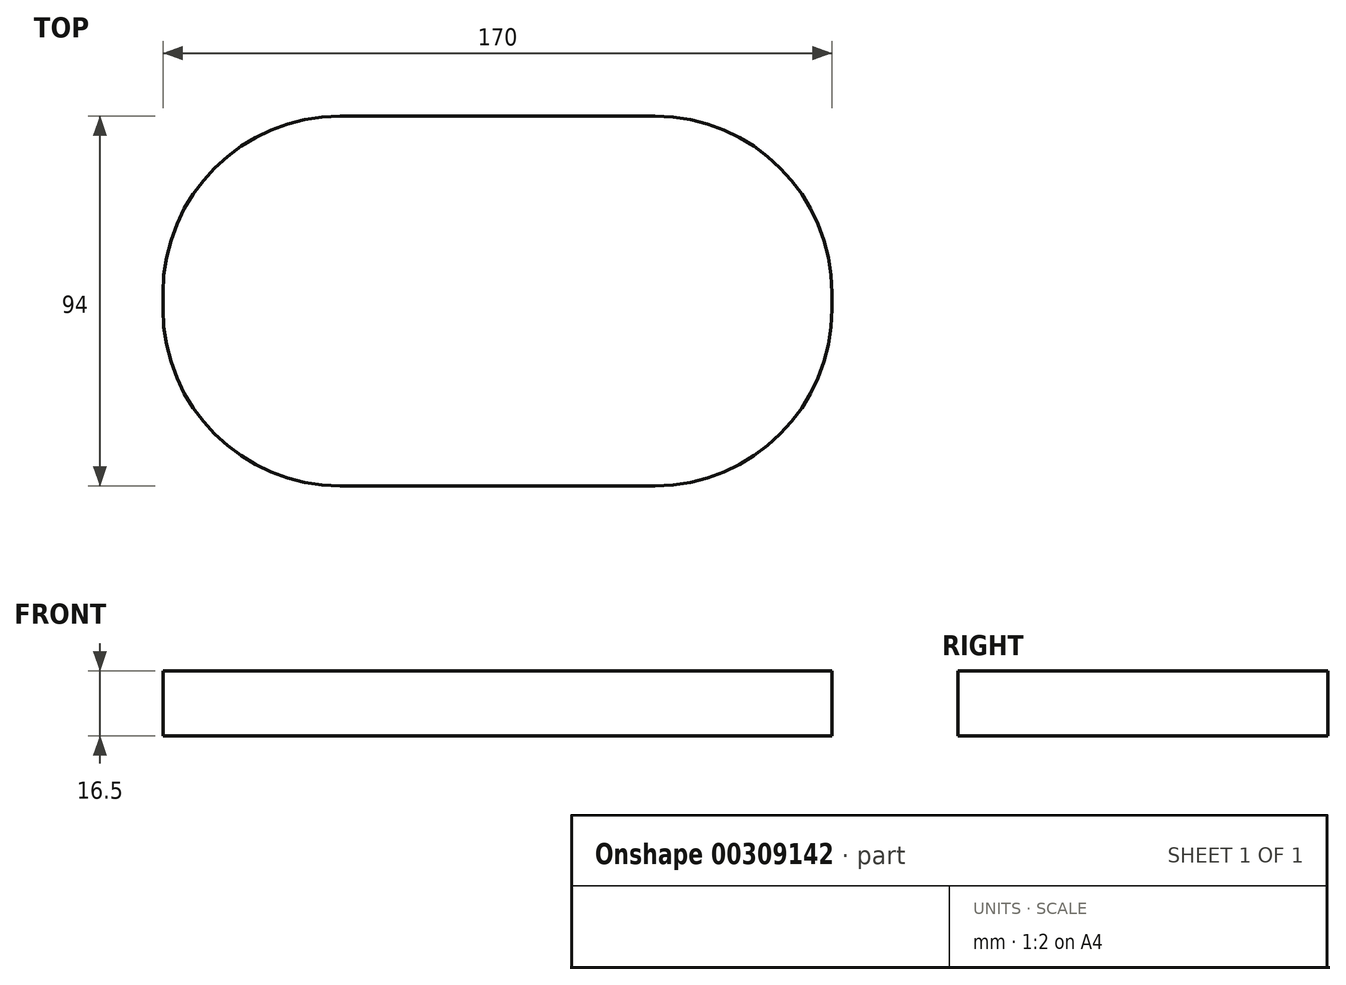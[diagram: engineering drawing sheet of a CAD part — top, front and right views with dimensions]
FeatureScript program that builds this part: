
annotation { "Feature Type Name" : "Feature", "Feature Type Description" : "" }
export const myFeature = defineFeature(function(context is Context, id is Id, definition is map)
    precondition{}
    {
        {
            var Q0;
            Q0=qCreatedBy(makeId("Top.planeOp"),FACE);
            var sketch = newSketch(context, id + "F0", { "sketchPlane" : qUnion([Q0])});
            skLineSegment(sketch, "E0.bottom", {"start": v(44.5, -51.5) * mm, "end": v(-44.5, -51.5) * mm});
            skLineSegment(sketch, "E0.top", {"start": v(44.5, 51.5) * mm, "end": v(-44.5, 51.5) * mm});
            skLineSegment(sketch, "E0.left", {"start": v(89.5, -6.5) * mm, "end": v(89.5, 6.5) * mm});
            skLineSegment(sketch, "E0.right", {"start": v(-89.5, -6.5) * mm, "end": v(-89.5, 6.5) * mm});
            skPoint(sketch, "E0.middle", {"position": v(0, 0) * mm});
            skPoint(sketch, "E1.visualSharp", {"position": v(89.5, 51.5) * mm});
            skArc(sketch, "E1.filletArc", {"start": v(89.5, 6.5) * mm, "mid": v(76.32, 38.32) * mm, "end": v(44.5, 51.5) * mm});
            skPoint(sketch, "E2.visualSharp", {"position": v(89.5, -51.5) * mm});
            skArc(sketch, "E2.filletArc", {"start": v(44.5, -51.5) * mm, "mid": v(76.32, -38.32) * mm, "end": v(89.5, -6.5) * mm});
            skPoint(sketch, "E3.visualSharp", {"position": v(-89.5, -51.5) * mm});
            skArc(sketch, "E3.filletArc", {"start": v(-89.5, -6.5) * mm, "mid": v(-76.32, -38.32) * mm, "end": v(-44.5, -51.5) * mm});
            skPoint(sketch, "E4.visualSharp", {"position": v(-89.5, 51.5) * mm});
            skArc(sketch, "E4.filletArc", {"start": v(-44.5, 51.5) * mm, "mid": v(-76.32, 38.32) * mm, "end": v(-89.5, 6.5) * mm});
            skSolve(sketch);
        }
        {
            var Q0;
            Q0=makeQuery(id+"F0.imprint","IMPRINT",FACE,{"disambiguationData":[TD([[makeQuery(id+"F0.imprint","IMPRINT",EDGE,{"derivedFrom":sQuery(id+"F0.wireOp",EDGE,"E0.bottom")}),-1.0]])]});
            var sketch = newSketch(context, id + "F1", { "sketchPlane" : qUnion([Q0])});
            skLineSegment(sketch, "E5.bottom", {"start": v(40, -47) * mm, "end": v(-40, -47) * mm});
            skLineSegment(sketch, "E5.top", {"start": v(40, 47) * mm, "end": v(-40, 47) * mm});
            skLineSegment(sketch, "E5.left", {"start": v(85, -2) * mm, "end": v(85, 2) * mm});
            skLineSegment(sketch, "E5.right", {"start": v(-85, -2) * mm, "end": v(-85, 2) * mm});
            skPoint(sketch, "E5.middle", {"position": v(0, 0) * mm});
            skPoint(sketch, "E6.visualSharp", {"position": v(85, 47) * mm});
            skArc(sketch, "E6.filletArc", {"start": v(85, 2) * mm, "mid": v(71.82, 33.82) * mm, "end": v(40, 47) * mm});
            skPoint(sketch, "E7.visualSharp", {"position": v(85, -47) * mm});
            skArc(sketch, "E7.filletArc", {"start": v(40, -47) * mm, "mid": v(71.82, -33.82) * mm, "end": v(85, -2) * mm});
            skPoint(sketch, "E8.visualSharp", {"position": v(-85, -47) * mm});
            skArc(sketch, "E8.filletArc", {"start": v(-85, -2) * mm, "mid": v(-71.82, -33.82) * mm, "end": v(-40, -47) * mm});
            skPoint(sketch, "E9.visualSharp", {"position": v(-85, 47) * mm});
            skArc(sketch, "E9.filletArc", {"start": v(-40, 47) * mm, "mid": v(-71.82, 33.82) * mm, "end": v(-85, 2) * mm});
            skSolve(sketch);
        }
        {
            var Q0;
            Q0 = qSketchRegion(id + "F1", true);
            extrude(context, id + "F2", {"entities" : qUnion([Q0]), "depth" : 16.5 * mm});
        }
        {
            var Q0;
            Q0 = qSketchRegion(id + "F0", true);
            extrude(context, id + "F3", {"entities" : qUnion([Q0]), "operationType" : NewBodyOperationType.INTERSECT, "depth" : 21 * mm});
        }
    });
